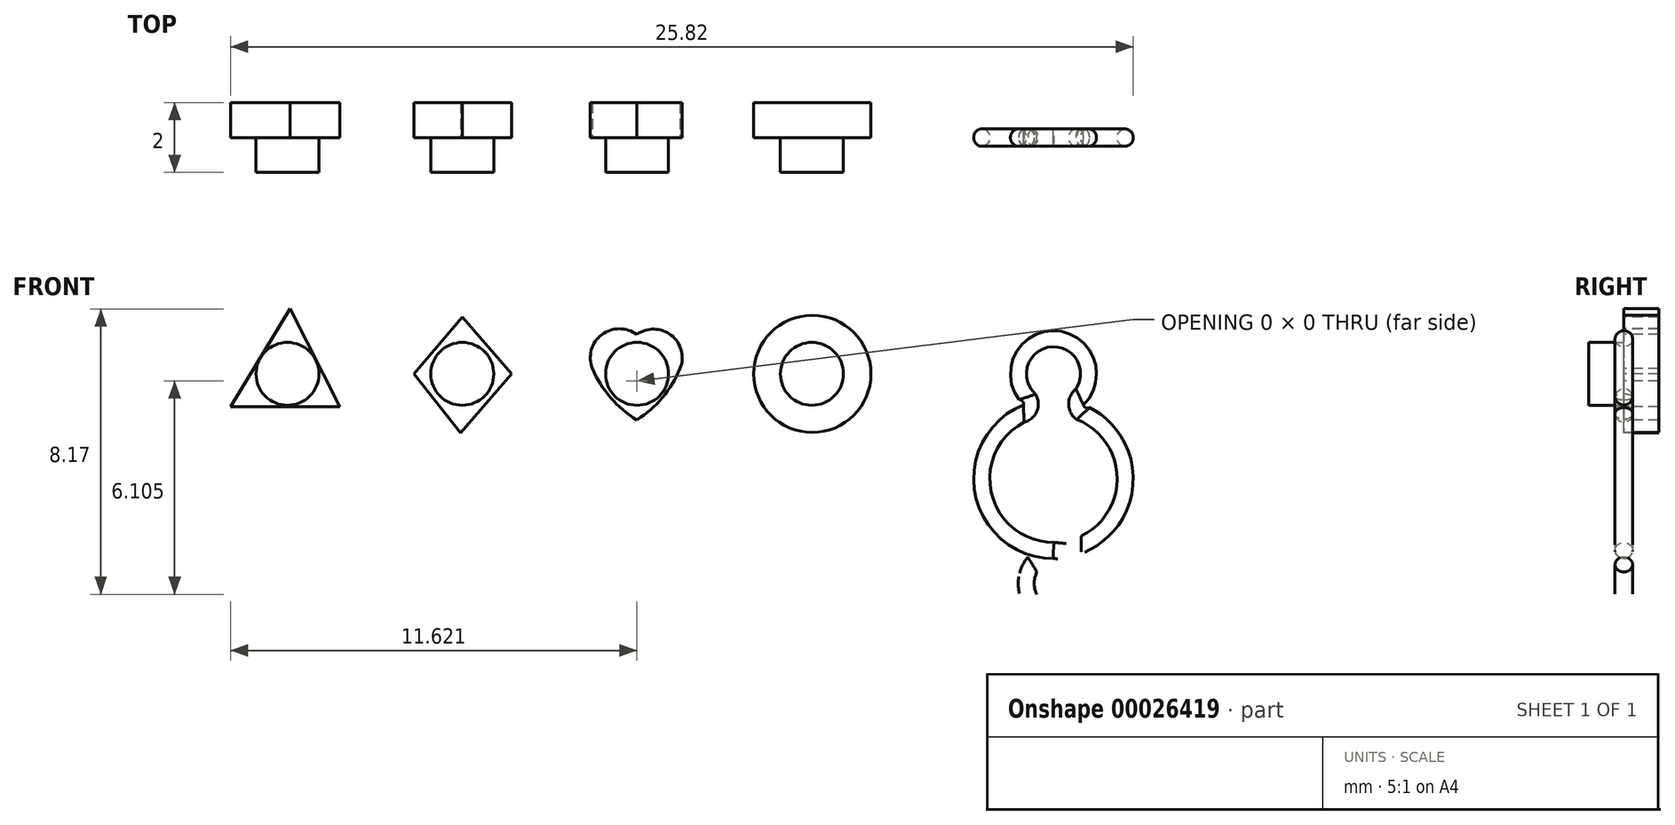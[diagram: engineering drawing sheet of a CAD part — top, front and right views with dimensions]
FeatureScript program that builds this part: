
annotation { "Feature Type Name" : "Feature", "Feature Type Description" : "" }
export const myFeature = defineFeature(function(context is Context, id is Id, definition is map)
    precondition{}
    {
        {
            var Q0;
            Q0=qCreatedBy(makeId("Front.planeOp"),FACE);
            var sketch = newSketch(context, id + "F0", { "sketchPlane" : qUnion([Q0])});
            skArc(sketch, "E0", {"start": v(0.75, -0.66) * mm, "mid": v(0, 1) * mm, "end": v(-0.75, -0.66) * mm});
            skArc(sketch, "E1", {"start": v(-0.85, -1.13) * mm, "mid": v(-2, -3.43) * mm, "end": v(0, -5.05) * mm});
            skPoint(sketch, "E2.visualSharp", {"position": v(-0.26, -0.97) * mm});
            skArc(sketch, "E2.filletArc", {"start": v(-0.85, -1.13) * mm, "mid": v(-0.68, -0.92) * mm, "end": v(-0.75, -0.66) * mm});
            skPoint(sketch, "E3.visualSharp", {"position": v(0.26, -0.97) * mm});
            skArc(sketch, "E3.filletArc", {"start": v(0.75, -0.66) * mm, "mid": v(0.68, -0.92) * mm, "end": v(0.85, -1.13) * mm});
            skArc(sketch, "E4.trimOffspring", {"start": v(0.8, -4.89) * mm, "mid": v(2.05, -3.03) * mm, "end": v(0.85, -1.13) * mm});
            skPoint(sketch, "E5.center.orphan", {"position": v(0, -6) * mm});
            skArc(sketch, "E6", {"start": v(-0.6, -5.46) * mm, "mid": v(0.53, -6.84) * mm, "end": v(0.24, -5.07) * mm});
            skLineSegment(sketch, "E7", {"start": v(0, -5.05) * mm, "end": v(0.24, -5.07) * mm});
            skSolve(sketch);
        }
        {
            var Q0;
            Q0=qCreatedBy(makeId("Right.planeOp"),FACE);
            cPlane(context, id + "F1", {"entities" : qUnion([Q0]), "cplaneType" : CPlaneType.OFFSET, "offset" : .8 * mm, "width" : 150 * mm, "height" : 150 * mm});
        }
        {
            var Q0;
            Q0=qCreatedBy(id+"F1.planeOp",FACE);
            var sketch = newSketch(context, id + "F2", { "sketchPlane" : qUnion([Q0])});
            skCircle(sketch, "E8", {"center": v(0, -4.89) * mm, "radius": 0.25 * mm});
            skSolve(sketch);
        }
        {
            var Q0;
            Q0 = qSketchRegion(id + "F2", true);
            var Q1;
            Q1=sQuery(id+"F0.wireOp",EDGE,"E4.trimOffspring");
            var Q2;
            Q2=sQuery(id+"F0.wireOp",EDGE,"E3.filletArc");
            var Q3;
            Q3=sQuery(id+"F0.wireOp",EDGE,"E0");
            var Q4;
            Q4=sQuery(id+"F0.wireOp",EDGE,"E2.filletArc");
            var Q5;
            Q5=sQuery(id+"F0.wireOp",EDGE,"E1");
            var Q6;
            Q6=sQuery(id+"F0.wireOp",EDGE,"E7");
            var Q7;
            Q7=sQuery(id+"F0.wireOp",EDGE,"E6");
            sweep(context, id + "F3", {"profiles" : qUnion([Q0]), "path" : qUnion([Q1, Q2, Q3, Q4, Q5, Q6, Q7])});
        }
        {
            var Q0;
            Q0=qCreatedBy(makeId("Front.planeOp"),FACE);
            var sketch = newSketch(context, id + "F4", { "sketchPlane" : qUnion([Q0])});
            skCircle(sketch, "E9", {"center": v(-21.91, 0) * mm, "radius": 0.9 * mm});
            skCircle(sketch, "E10", {"center": v(-16.91, 0) * mm, "radius": 0.9 * mm});
            skCircle(sketch, "E11", {"center": v(-11.91, 0) * mm, "radius": 0.9 * mm});
            skCircle(sketch, "E12", {"center": v(-6.91, 0) * mm, "radius": 0.9 * mm});
            skSolve(sketch);
        }
        {
            var Q0;
            Q0 = qSketchRegion(id + "F4", true);
            extrude(context, id + "F5", {"entities" : qUnion([Q0]), "depth" : 1 * mm});
        }
        {
            var Q0;
            Q0=qCreatedBy(makeId("Front.planeOp"),FACE);
            var sketch = newSketch(context, id + "F6", { "sketchPlane" : qUnion([Q0])});
            skCircle(sketch, "E13", {"center": v(-6.9, 0) * mm, "radius": 1.68 * mm});
            skArc(sketch, "E14", {"start": v(-10.68, 0.15) * mm, "mid": v(-10.93, 1.1) * mm, "end": v(-11.92, 1.12) * mm});
            skArc(sketch, "E15", {"start": v(-11.92, -0.2) * mm, "mid": v(-11.92, -0.2) * mm, "end": v(-11.92, -0.2) * mm});
            skArc(sketch, "E16", {"start": v(-11.92, -1.32) * mm, "mid": v(-11.19, -0.68) * mm, "end": v(-10.68, 0.15) * mm});
            skArc(sketch, "E17", {"start": v(-13.2, 0.15) * mm, "mid": v(-12.67, -0.68) * mm, "end": v(-11.92, -1.32) * mm});
            skArc(sketch, "E18.trimOffspring", {"start": v(-11.92, 1.12) * mm, "mid": v(-12.92, 1.12) * mm, "end": v(-13.2, 0.15) * mm});
            skLineSegment(sketch, "E19.trimOffspring", {"start": v(-11.92, -0.2) * mm, "end": v(-11.92, -0.2) * mm});
            skLineSegment(sketch, "E20", {"start": v(-15.5, 0) * mm, "end": v(-16.91, 1.62) * mm});
            skLineSegment(sketch, "E21", {"start": v(-16.91, 1.62) * mm, "end": v(-18.29, 0) * mm});
            skLineSegment(sketch, "E22", {"start": v(-18.29, 0) * mm, "end": v(-16.96, -1.7) * mm});
            skLineSegment(sketch, "E23", {"start": v(-16.96, -1.7) * mm, "end": v(-15.5, 0) * mm});
            skLineSegment(sketch, "E24", {"start": v(-21.83, 1.86) * mm, "end": v(-20.41, -0.93) * mm});
            skLineSegment(sketch, "E25", {"start": v(-20.41, -0.93) * mm, "end": v(-23.54, -0.93) * mm});
            skLineSegment(sketch, "E26", {"start": v(-23.54, -0.93) * mm, "end": v(-21.83, 1.86) * mm});
            skSolve(sketch);
        }
        {
            var Q0;
            Q0 = qSketchRegion(id + "F6", true);
            extrude(context, id + "F7", {"entities" : qUnion([Q0]), "oppositeDirection" : true, "depth" : 1 * mm});
        }
    });
